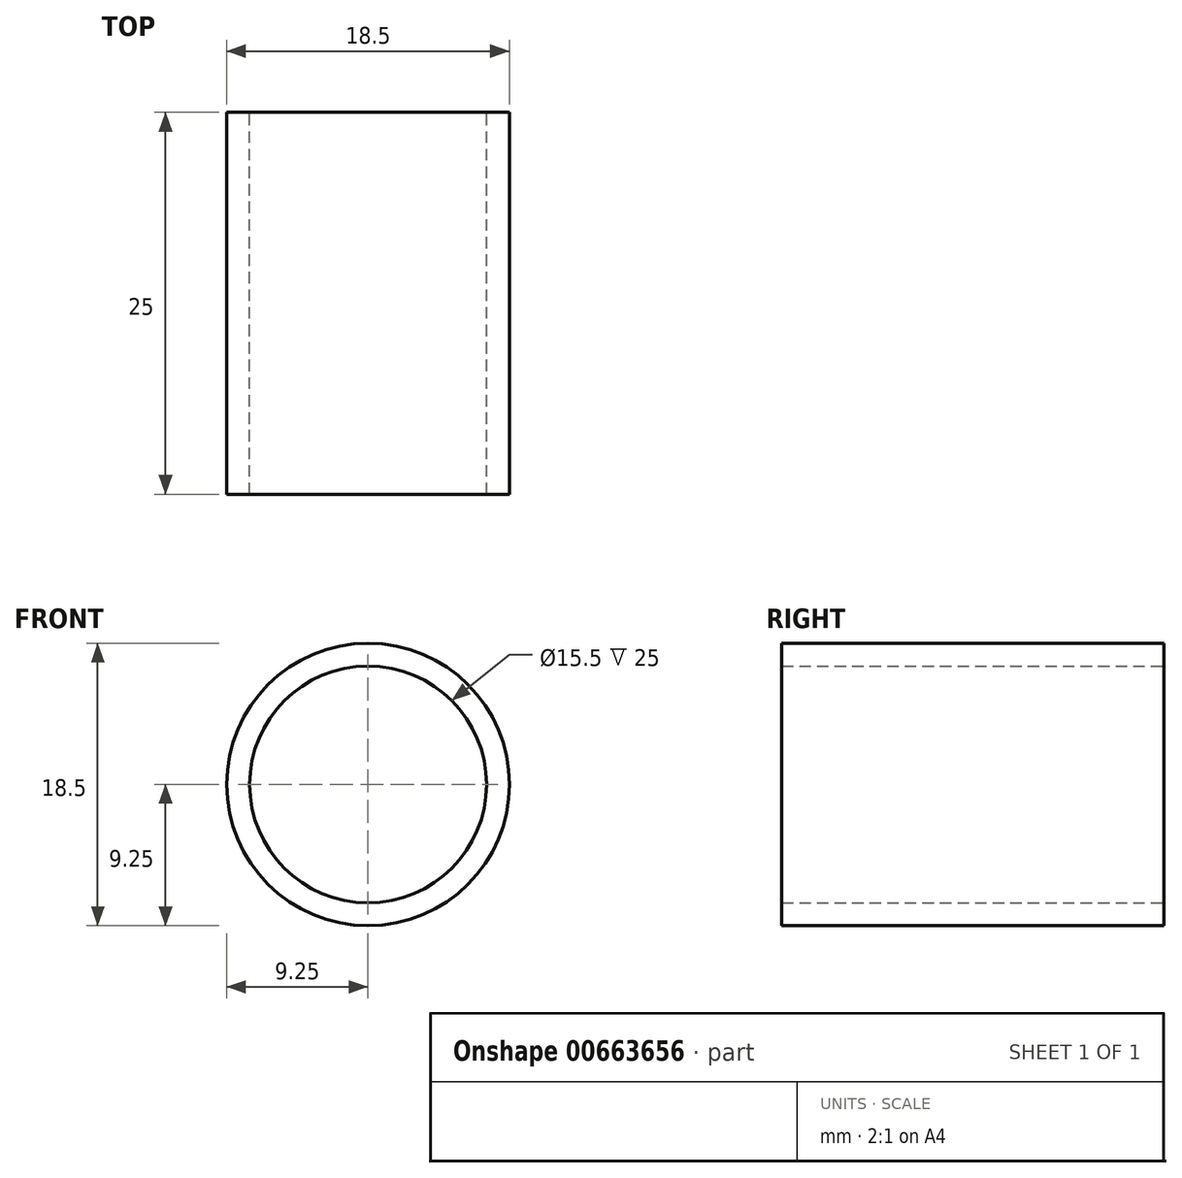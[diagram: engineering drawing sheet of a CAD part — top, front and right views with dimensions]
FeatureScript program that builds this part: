
annotation { "Feature Type Name" : "Feature", "Feature Type Description" : "" }
export const myFeature = defineFeature(function(context is Context, id is Id, definition is map)
    precondition{}
    {
        {
            var Q0;
            Q0=qCreatedBy(makeId("Front.planeOp"),FACE);
            var sketch = newSketch(context, id + "F0", { "sketchPlane" : qUnion([Q0])});
            skCircle(sketch, "E0", {"center": v(0, 0) * mm, "radius": 9.25 * mm});
            skCircle(sketch, "E1.0", {"center": v(0, 0) * mm, "radius": 7.75 * mm});
            skSolve(sketch);
        }
        {
            var Q0;
            Q0=qSketchRegion(id+"F0",true);
            extrude(context, id + "F1", {"entities" : qUnion([Q0]), "depth" : 25 * mm, "offsetDistance" : 25 * mm});
        }
    });
